# Revit family: TAG1
name_source: partatom
category: Furniture
units: mm (PartAtom-declared; Revit-internal decimal feet)

## family parameters
Always vertical = Yes
Cut with Voids When Loaded = No
OmniClass Number = 23.40.20.00
OmniClass Title = General Furniture and Specialties
Render Appearance Source = Family Geometry
Room Calculation Point = No
Shared = No
Work Plane-Based = No

## types (1)
- CW005
    Default Elevation = 0 mm  [stored 0 ft]
    Description = 1 x CaseWorks Backsplash Laminate 04Hx66W, 3 x CaseWorks Backsplash Laminate 04Hx84W, 1 x CaseWorks Countertop Laminate 24Dx66W, 3 x CaseWorks Countertop Laminate 24Dx84W, 1 x CaseWorks Toe Kick 04Hx30W (Cut to size on-site), 3 x CaseWorks Toe Kick 04Hx84W (Cut to size on-site), 3 x CaseWorks Side Toe Kick 04Hx20.22W (Cut to size on-site), 1 x CaseWorks Base Cab Single Door & Drawer Right 33Hx18Wx24D, 3 x CaseWorks Base Cab Double Doors Single Drawer 33Hx36Wx24D, 1 x CaseWorks Base Appliance Garage Cabinet 33Hx36Wx24D, 1 x CaseWorks Base Cabinet Four Drawers 33Hx30Wx24D, 2 x CaseWorks Base Cabinet Four Drawers 33Hx30Wx24D, 1 x CaseWorks Base Cabinet Single Drawer w Cubby 33Hx30Wx24D, 2 x CaseWorks Base Cabinet Trash Pullout 33Hx18Wx24D, 1 x CaseWorks Wood Wall Cleat - 72" (Cut to size on-site), 1 x CaseWorks Wood Wall Cleat - 96" (Cut to size on-site), 1 x CaseWorks Wall Cabinet Single Door Left 30Hx18Wx15D, 2 x CaseWorks Wall Cabinet Double Door 30Hx30Wx15D, 1 x CaseWorks Wall Cabinet Single Door Right 30Hx18Wx15D, 2 x CaseWorks Wall Cabinet Open 30Hx36Wx15D, 6 x Soft Close Mechanism for Hinged Doors, 1 x Cbx Tackboard Wall Mount 35hx72w, 1 x Cbx Tackboard Wall Mount 35hx78w
    Exported From CET Designer = Yes
    Manufacturer = AIS
    Model = M-ABL0466
    Show CW005 = Yes
    VisibilityIndex = 0

note: [stored X ft] marks values corroborated as IEEE doubles in the binary element streams (Revit-internal decimal feet)

## geometry (parser evidence)
native form markers: Sweep x2
no freeform markers — native parametric forms only
